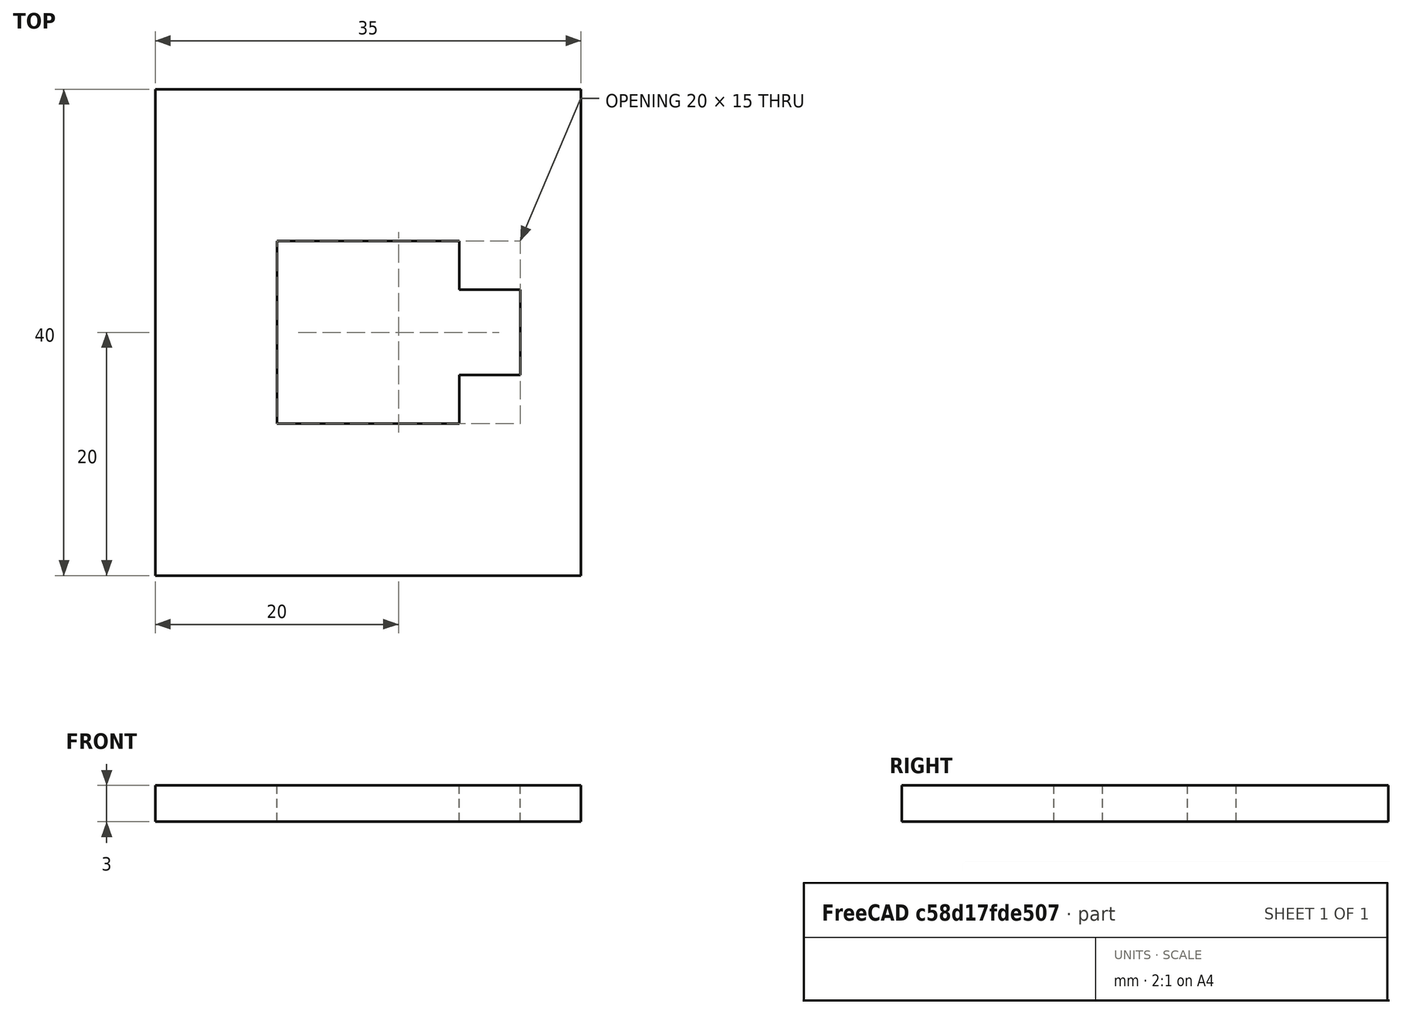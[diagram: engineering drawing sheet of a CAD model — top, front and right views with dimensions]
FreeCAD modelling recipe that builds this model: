
FCSTD DOCUMENT  (FreeCAD 0.21R33771 (Git))
Label: Pata
License: All rights reserved
LicenseURL: http://en.wikipedia.org/wiki/All_rights_reserved
objects: Sketcher::SketchObject×1, Part::Extrusion×1
note: 2 computed .brp shape members not serialized (recipe doc carries the construction recipe); baked Part::Feature solids carry a one-line shape summary decoded from their .brp

FEATURE [Sketcher::SketchObject] Sketch
  FullyConstrained = true
  sketch-geometry (14):
    g0: LineSegment StartX=-17.5 StartY=-20 StartZ=0 EndX=-17.5 EndY=20 EndZ=0
    g1: LineSegment StartX=-17.5 StartY=20 StartZ=0 EndX=17.5 EndY=20 EndZ=0
    g2: LineSegment StartX=17.5 StartY=20 StartZ=0 EndX=17.5 EndY=-20 EndZ=0
    g3: LineSegment StartX=17.5 StartY=-20 StartZ=0 EndX=-17.5 EndY=-20 EndZ=0
    g4: GeomPoint X=0 Y=0 Z=0
    g5: LineSegment StartX=-7.5 StartY=-7.5 StartZ=0 EndX=-7.5 EndY=7.5 EndZ=0
    g6: LineSegment StartX=-7.5 StartY=7.5 StartZ=0 EndX=7.5 EndY=7.5 EndZ=0
    g7: LineSegment StartX=7.5 StartY=7.5 StartZ=0 EndX=7.5 EndY=3.5 EndZ=0
    g8: LineSegment StartX=7.5 StartY=-7.5 StartZ=0 EndX=-7.5 EndY=-7.5 EndZ=0
    g9: GeomPoint X=0 Y=0 Z=0
    g10: LineSegment StartX=7.5 StartY=3.5 StartZ=0 EndX=12.5 EndY=3.5 EndZ=0
    g11: LineSegment StartX=12.5 StartY=3.5 StartZ=0 EndX=12.5 EndY=-3.5 EndZ=0
    g12: LineSegment StartX=12.5 StartY=-3.5 StartZ=0 EndX=7.5 EndY=-3.5 EndZ=0
    g13: LineSegment StartX=7.5 StartY=-3.5 StartZ=0 EndX=7.5 EndY=-7.5 EndZ=0
  constraints (37):
    c: Coincident(g0,g1)
    c: Coincident(g1,g2)
    c: Coincident(g2,g3)
    c: Coincident(g3,g0)
    c: Horizontal(g1)
    c: Horizontal(g3)
    c: Vertical(g0)
    c: Vertical(g2)
    c: Symmetric(g1,g0,g4)
    c: PointOnObject(g4,g-2)
    c: Coincident(g5,g6)
    c: Coincident(g6,g7)
    c: Coincident(g13,g8)
    c: Coincident(g8,g5)
    c: Horizontal(g6)
    c: Horizontal(g8)
    c: Vertical(g5)
    c: Vertical(g7)
    c: Symmetric(g6,g5,g9)
    c: Coincident(g9,g-1)
    c: Distance(g1) = 35
    c: Distance(g2) = 40
    c: PointOnObject(g4,g-1)
    c: Horizontal(g10)
    c: Coincident(g11,g10)
    c: Vertical(g11)
    c: Coincident(g12,g11)
    c: Horizontal(g12)
    c: Coincident(g7,g10)
    c: Coincident(g13,g12)
    c: Distance(g6) = 15
    c: Distance(g5) = 15
    c: Distance(g8) = 15
    c: Vertical(g13)
    c: Equal(g7,g13)
    c: Distance(g7) = 4
    c: Distance(g12) = 5
FEATURE [Part::Extrusion] Extrude
  Base = -> Sketch
  Dir = (0,0,1)
  DirMode = 2
  FaceMakerClass = Part::FaceMakerBullseye
  LengthFwd = 3
  LengthRev = 0
  Solid = true
  Symmetric = false
